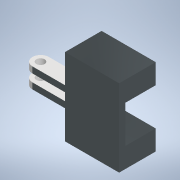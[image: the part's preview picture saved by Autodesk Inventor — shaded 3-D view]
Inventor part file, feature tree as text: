
AUTODESK INVENTOR PART (.ipt)
format: ipt  version: 2022 (Build 260153000, 153)  size: 215,040 bytes
history: native  units: mm
features: extrude x6, sketch x5, other x5, reference x4, fillet x1
ambient origin geometry x8: Origin, YZ Plane, XZ Plane, XY Plane, X Axis, Y Axis, Z Axis, Center Point
bodies: Solid1 (feature_tree)
feature tree (21):
  extrude  "Extrusion1"  Depth=0.3mm
  extrude  "Extrusion3"  Depth=0.3mm
  sketch  "Sketch5"  dims[d4=0.3mm d5=24.4mm]
  extrude  "Extrusion4"  Depth=24.4mm
  extrude  "Extrusion5"  Depth=3.0mm
  extrude  "Extrusion8"  Depth=3.0mm TaperAngle=0.0deg
  fillet  "Fillet1"  Radius=4.0mm
  extrude  "Extrusion9"  Depth=4.0mm
  sketch  "Sketch1"  dims[d0=0.3mm d1=0.3mm]
  reference  "Reference1"
  reference  "Reference2"
  reference  "Reference3"
  reference  "Reference4"
  sketch  "Sketch4"  dims[d2=0.3mm d3=0.3mm]
  sketch  "Sketch16"  dims[d6=3.8mm d7=3.0mm]
  sketch  "Sketch17"  dims[d8=15.0mm d9=0.0mm d12=3.0mm d13=0.0mm d14=4.0mm d15=6.0mm d16=8.0mm d17=9.2mm d18=1.0mm d19=0.0mm d20=80.0mm d21=0.0mm d41=3.0mm d42=1.9mm d43=8.06mm d44=20.03mm d45=0.0mm d46=4.0mm d47=4.06mm d48=20.0mm d49=0.0mm d36=0.5mm d37=0.872665mm d38=0.5mm d39=0.872665mm]
  other  "<userpath>\OneDrive\Escritorio\Mini_Proyecto_Diseno\Diseno_18012\Modelo_MPD\Carril.iam"
  other  "Carril.iam"
  other  "Lateral_Carril:2"
  other  "Lateral_Carril:1"
  other  "Base_Carril:1"
